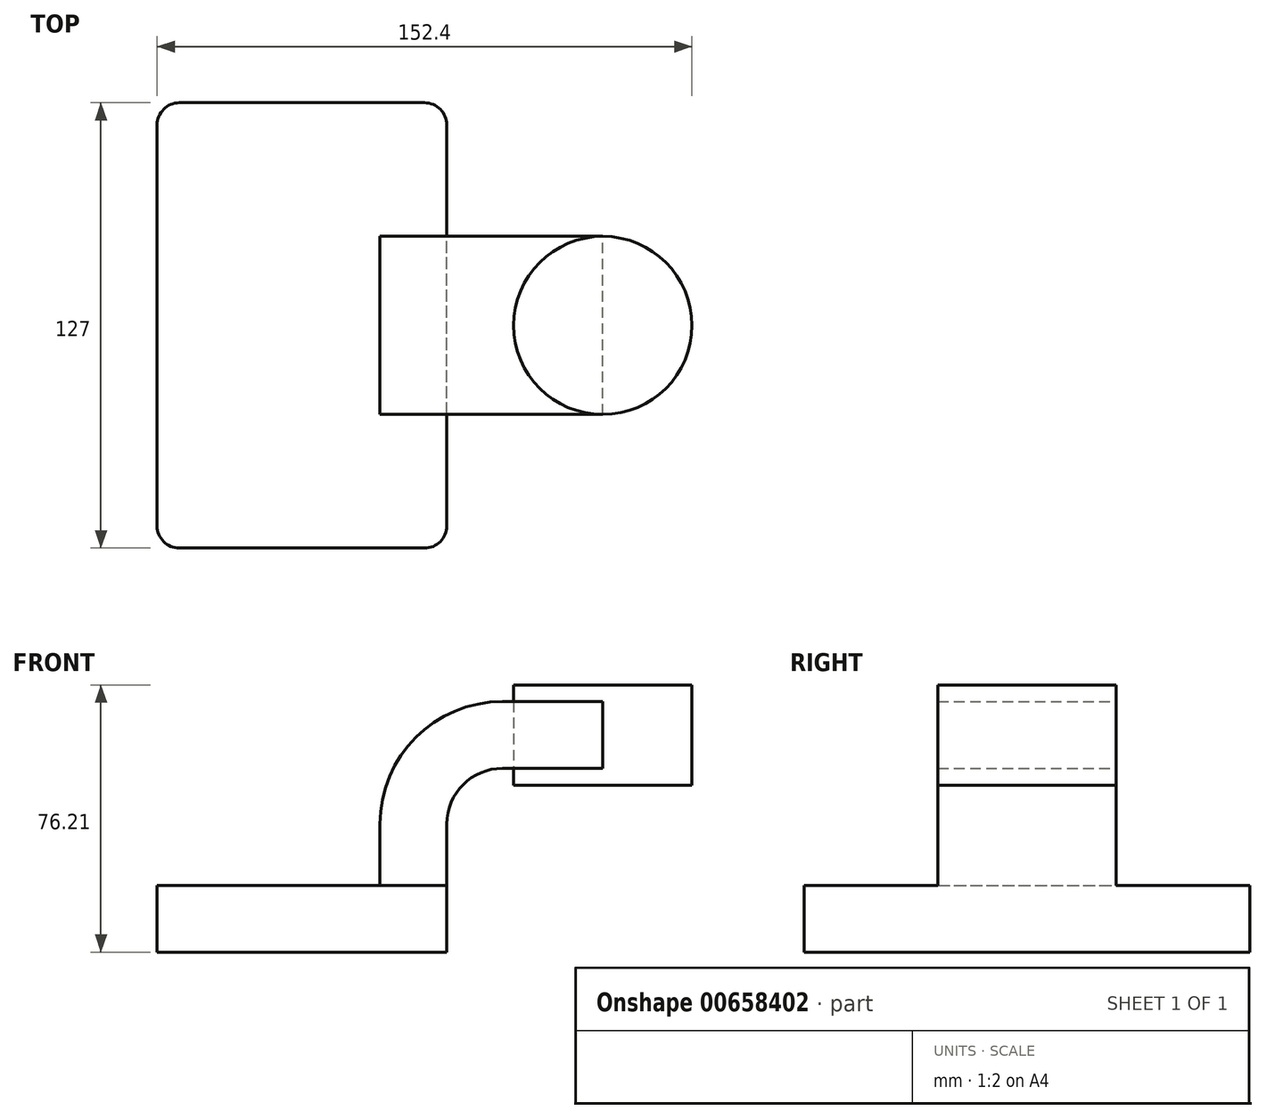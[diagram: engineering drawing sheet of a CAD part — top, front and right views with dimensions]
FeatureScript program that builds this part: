
annotation { "Feature Type Name" : "Feature", "Feature Type Description" : "" }
export const myFeature = defineFeature(function(context is Context, id is Id, definition is map)
    precondition{}
    {
        {
            var Q0;
            Q0=qCreatedBy(makeId("Front.planeOp"),FACE);
            var sketch = newSketch(context, id + "F0", { "sketchPlane" : qUnion([Q0])});
            skLineSegment(sketch, "E0.bottom", {"start": v(-41.28, 9.52) * mm, "end": v(41.27, 9.53) * mm});
            skLineSegment(sketch, "E0.top", {"start": v(-41.28, -9.52) * mm, "end": v(41.28, -9.52) * mm});
            skLineSegment(sketch, "E0.left", {"start": v(-41.28, 9.52) * mm, "end": v(-41.28, -9.53) * mm});
            skLineSegment(sketch, "E0.right", {"start": v(41.27, 9.53) * mm, "end": v(41.28, -9.52) * mm});
            skPoint(sketch, "E0.middle", {"position": v(0, 0) * mm});
            skLineSegment(sketch, "E1.bottom", {"start": v(60.32, 38.1) * mm, "end": v(111.12, 38.1) * mm});
            skLineSegment(sketch, "E1.top", {"start": v(60.32, 66.68) * mm, "end": v(111.12, 66.68) * mm});
            skLineSegment(sketch, "E1.left", {"start": v(60.32, 38.1) * mm, "end": v(60.32, 66.68) * mm});
            skLineSegment(sketch, "E1.right", {"start": v(111.12, 38.1) * mm, "end": v(111.12, 66.68) * mm});
            skPoint(sketch, "E1.middle", {"position": v(85.72, 52.39) * mm});
            skLineSegment(sketch, "E2", {"start": v(41.27, 9.53) * mm, "end": v(41.27, 27) * mm});
            skArc(sketch, "E3", {"start": v(41.27, 27) * mm, "mid": v(45.92, 38.23) * mm, "end": v(57.15, 42.88) * mm});
            skLineSegment(sketch, "E4", {"start": v(57.15, 42.88) * mm, "end": v(85.73, 42.88) * mm});
            skLineSegment(sketch, "E5.0", {"start": v(57.15, 61.93) * mm, "end": v(85.72, 61.93) * mm});
            skArc(sketch, "E5.1", {"start": v(22.22, 27) * mm, "mid": v(32.45, 51.7) * mm, "end": v(57.15, 61.93) * mm});
            skLineSegment(sketch, "E5.2", {"start": v(22.22, 9.53) * mm, "end": v(22.22, 27) * mm});
            skFitSpline(sketch, "E6", {"points": [v(-41.28, 9.52) * mm, v(57.15, 61.93) * mm], "startDerivative": vector(23.04, 120.47) * mm, "endDerivative": vector(108.94, -5.9) * mm});
            skLineSegment(sketch, "E7", {"start": v(85.72, 38.1) * mm, "end": v(85.72, 66.68) * mm});
            skSolve(sketch);
        }
        {
            var Q0;
            Q0=makeQuery(id+"F0.imprint","IMPRINT",FACE,{"disambiguationData":[TD([[makeQuery(id+"F0.imprint","IMPRINT",EDGE,{"derivedFrom":sQuery(id+"F0.wireOp",EDGE,"E0.top")}),1.0]])]});
            extrude(context, id + "F1", {"entities" : qUnion([Q0]), "endBound" : BoundingType.SYMMETRIC, "depth" : 127 * mm, "offsetDistance" : 25.4 * mm});
        }
        {
            var Q0;
            {var subQ1=sQuery(id+"F0.wireOp",EDGE,"E2");Q0=makeQuery(id+"F0.imprint","IMPRINT",FACE,{"disambiguationData":[TD([[makeQuery(id+"F0.imprint","IMPRINT",EDGE,{"derivedFrom":subQ1}),1.0]])]});}
            var Q1;
            {var subQ0=sQuery(id+"F0.wireOp",EDGE,"E4");var subQ1=sQuery(id+"F0.wireOp",EDGE,"E1.left");var subQ2=makeQuery(id+"F0.imprint","INTERSECT",VERTEX,{"derivedFrom":[subQ1,subQ0]});Q1=makeQuery(id+"F0.imprint","IMPRINT",FACE,{"disambiguationData":[TD([[makeQuery(id+"F0.imprint","IMPRINT",EDGE,{"disambiguationData":[TD([[subQ2,-1.0]])],"derivedFrom":subQ1}),-1.0]])]});}
            extrude(context, id + "F2", {"entities" : qUnion([Q0, Q1]), "operationType" : NewBodyOperationType.ADD, "endBound" : BoundingType.SYMMETRIC, "depth" : 50.8 * mm, "offsetDistance" : 25.4 * mm});
        }
        {
            var Q0;
            Q0=makeQuery(id+"F0.imprint","IMPRINT",FACE,{"disambiguationData":[TD([[makeQuery(id+"F0.imprint","IMPRINT",EDGE,{"derivedFrom":sQuery(id+"F0.wireOp",EDGE,"E5.1")}),1.0]])]});
            extrude(context, id + "F3", {"entities" : qUnion([Q0]), "operationType" : NewBodyOperationType.ADD, "endBound" : BoundingType.SYMMETRIC, "depth" : 15.88 * mm, "offsetDistance" : 25.4 * mm});
        }
        {
            var Q0;
            {var subQ4=sQuery(id+"F0.wireOp",EDGE,"E1.right");Q0=makeQuery(id+"F0.imprint","IMPRINT",FACE,{"disambiguationData":[TD([[makeQuery(id+"F0.imprint","IMPRINT",EDGE,{"derivedFrom":subQ4}),1.0]])]});}
            var Q1;
            Q1=sQuery(id+"F0.wireOp",EDGE,"E7");
            revolve(context, id + "F4", {"entities" : qUnion([Q0]), "axis" : qUnion([Q1]), "revolveType" : RevolveType.FULL});
        }
        {
            var Q0;
            Q0=makeQuery(id+"F1.opExtrude","CAP_EDGE",EDGE,{"disambiguationData":[OSD([sQuery(id+"F0.wireOp",EDGE,"E0.left")])],"isStart":false});
            var Q1;
            Q1=makeQuery(id+"F1.opExtrude","CAP_EDGE",EDGE,{"disambiguationData":[OSD([sQuery(id+"F0.wireOp",EDGE,"E0.right")])],"isStart":false});
            var Q2;
            Q2=makeQuery(id+"F1.opExtrude","CAP_EDGE",EDGE,{"disambiguationData":[OSD([sQuery(id+"F0.wireOp",EDGE,"E0.right")])],"isStart":true});
            var Q3;
            Q3=makeQuery(id+"F1.opExtrude","CAP_EDGE",EDGE,{"disambiguationData":[OSD([sQuery(id+"F0.wireOp",EDGE,"E0.left")])],"isStart":true});
            fillet(context, id + "F5", {"entities" : qUnion([Q0, Q1, Q2, Q3]), "radius" : 6.35 * mm, "tangentPropagation" : true, "allowEdgeOverflow" : false});
        }
    });
